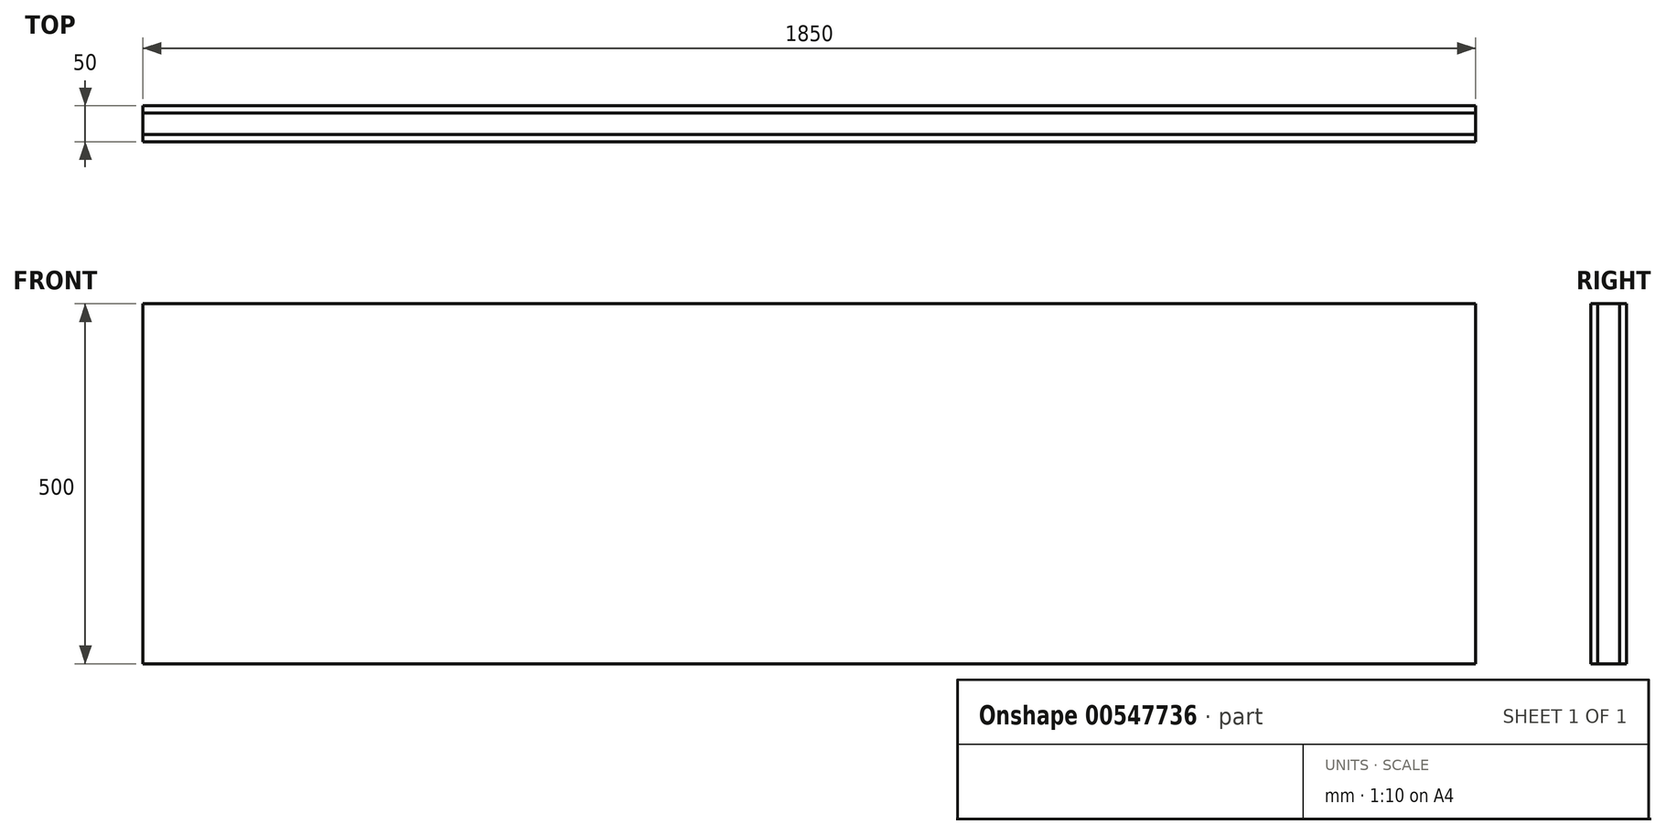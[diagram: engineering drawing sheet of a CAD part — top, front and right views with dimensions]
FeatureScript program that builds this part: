
annotation { "Feature Type Name" : "Feature", "Feature Type Description" : "" }
export const myFeature = defineFeature(function(context is Context, id is Id, definition is map)
    precondition{}
    {
        {
            var Q0;
            Q0=qCreatedBy(makeId("Top.planeOp"),FACE);
            var sketch = newSketch(context, id + "F0", { "sketchPlane" : qUnion([Q0])});
            skLineSegment(sketch, "E0.bottom", {"start": v(925, 15) * mm, "end": v(-925, 15) * mm});
            skLineSegment(sketch, "E0.top", {"start": v(925, -15) * mm, "end": v(-925, -15) * mm});
            skLineSegment(sketch, "E0.left", {"start": v(925, 15) * mm, "end": v(925, -15) * mm});
            skLineSegment(sketch, "E0.right", {"start": v(-925, 15) * mm, "end": v(-925, -15) * mm});
            skPoint(sketch, "E0.middle", {"position": v(0, 0) * mm});
            skSolve(sketch);
        }
        {
            var Q0;
            Q0 = qSketchRegion(id + "F0", true);
            extrude(context, id + "F1", {"entities" : qUnion([Q0]), "endBound" : BoundingType.SYMMETRIC, "depth" : 500 * mm, "offsetDistance" : 25 * mm});
        }
        {
            var Q0;
            Q0=makeQuery(id+"F1.opExtrude","SWEPT_FACE",FACE,{"disambiguationData":[OSD([sQuery(id+"F0.wireOp",EDGE,"E0.top")])]});
            var sketch = newSketch(context, id + "F2", { "sketchPlane" : qUnion([Q0])});
            skLineSegment(sketch, "E1.0", {"start": v(925, 250) * mm, "end": v(-925, 250) * mm});
            skLineSegment(sketch, "E2.0", {"start": v(-925, 250) * mm, "end": v(-925, -250) * mm});
            skLineSegment(sketch, "E3.0", {"start": v(925, -250) * mm, "end": v(-925, -250) * mm});
            skLineSegment(sketch, "E4.0", {"start": v(925, 250) * mm, "end": v(925, -250) * mm});
            skSolve(sketch);
        }
        {
            var Q0;
            Q0 = qSketchRegion(id + "F2", true);
            extrude(context, id + "F3", {"entities" : qUnion([Q0]), "depth" : 10 * mm, "offsetDistance" : 25 * mm});
        }
        {
            var Q0;
            Q0=makeQuery(id+"F1.opExtrude","SWEPT_FACE",FACE,{"disambiguationData":[OSD([sQuery(id+"F0.wireOp",EDGE,"E0.bottom")])]});
            var sketch = newSketch(context, id + "F4", { "sketchPlane" : qUnion([Q0])});
            skLineSegment(sketch, "E5.0", {"start": v(-925, 250) * mm, "end": v(925, 250) * mm});
            skLineSegment(sketch, "E6.0", {"start": v(-925, 250) * mm, "end": v(-925, -250) * mm});
            skLineSegment(sketch, "E7.0", {"start": v(-925, -250) * mm, "end": v(925, -250) * mm});
            skLineSegment(sketch, "E8.0", {"start": v(925, 250) * mm, "end": v(925, -250) * mm});
            skSolve(sketch);
        }
        {
            var Q0;
            Q0 = qSketchRegion(id + "F4", true);
            extrude(context, id + "F5", {"entities" : qUnion([Q0]), "depth" : 10 * mm, "offsetDistance" : 25 * mm});
        }
    });
